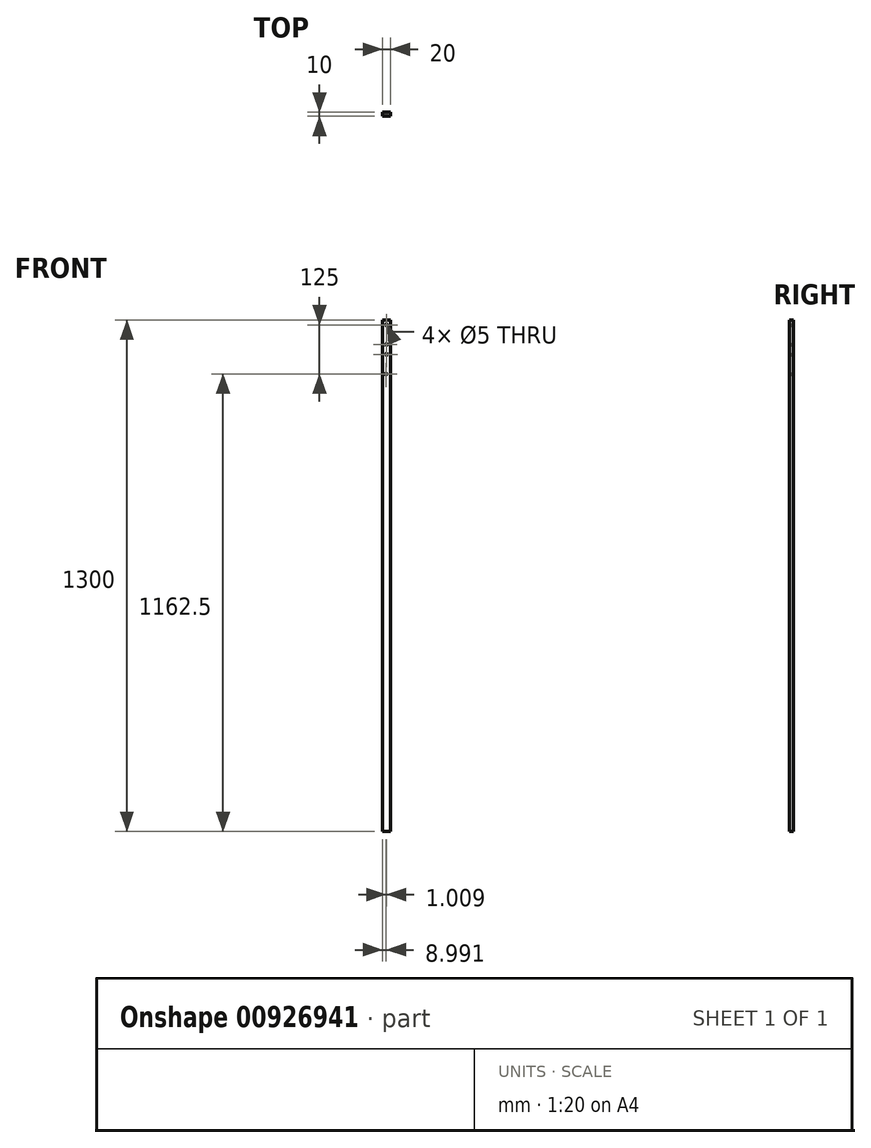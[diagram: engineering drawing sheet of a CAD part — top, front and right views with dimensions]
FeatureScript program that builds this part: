
annotation { "Feature Type Name" : "Feature", "Feature Type Description" : "" }
export const myFeature = defineFeature(function(context is Context, id is Id, definition is map)
    precondition{}
    {
        {
            var Q0;
            Q0=qCreatedBy(makeId("Front.planeOp"),FACE);
            var sketch = newSketch(context, id + "F0", { "sketchPlane" : qUnion([Q0])});
            skLineSegment(sketch, "E0.bottom", {"start": v(10, 650) * mm, "end": v(-10, 650) * mm});
            skLineSegment(sketch, "E0.top", {"start": v(10, -650) * mm, "end": v(-10, -650) * mm});
            skLineSegment(sketch, "E0.left", {"start": v(10, 650) * mm, "end": v(10, -650) * mm});
            skLineSegment(sketch, "E0.right", {"start": v(-10, 650) * mm, "end": v(-10, -650) * mm});
            skPoint(sketch, "E0.middle", {"position": v(0, 0) * mm});
            skCircle(sketch, "E1", {"center": v(0, 637.5) * mm, "radius": 2.5 * mm});
            skCircle(sketch, "E2", {"center": v(-0.2, 587.5) * mm, "radius": 2.5 * mm});
            skCircle(sketch, "E3", {"center": v(0, 562.5) * mm, "radius": 2.5 * mm});
            skCircle(sketch, "E4", {"center": v(-1, 512.5) * mm, "radius": 2.5 * mm});
            skSolve(sketch);
        }
        {
            var Q0;
            Q0=makeQuery(id+"F0.imprint","IMPRINT",FACE,{"disambiguationData":[TD([[makeQuery(id+"F0.imprint","IMPRINT",EDGE,{"derivedFrom":sQuery(id+"F0.wireOp",EDGE,"E0.bottom")}),1.0]])]});
            extrude(context, id + "F1", {"entities" : qUnion([Q0]), "depth" : 10 * mm, "offsetDistance" : 25 * mm});
        }
    });
